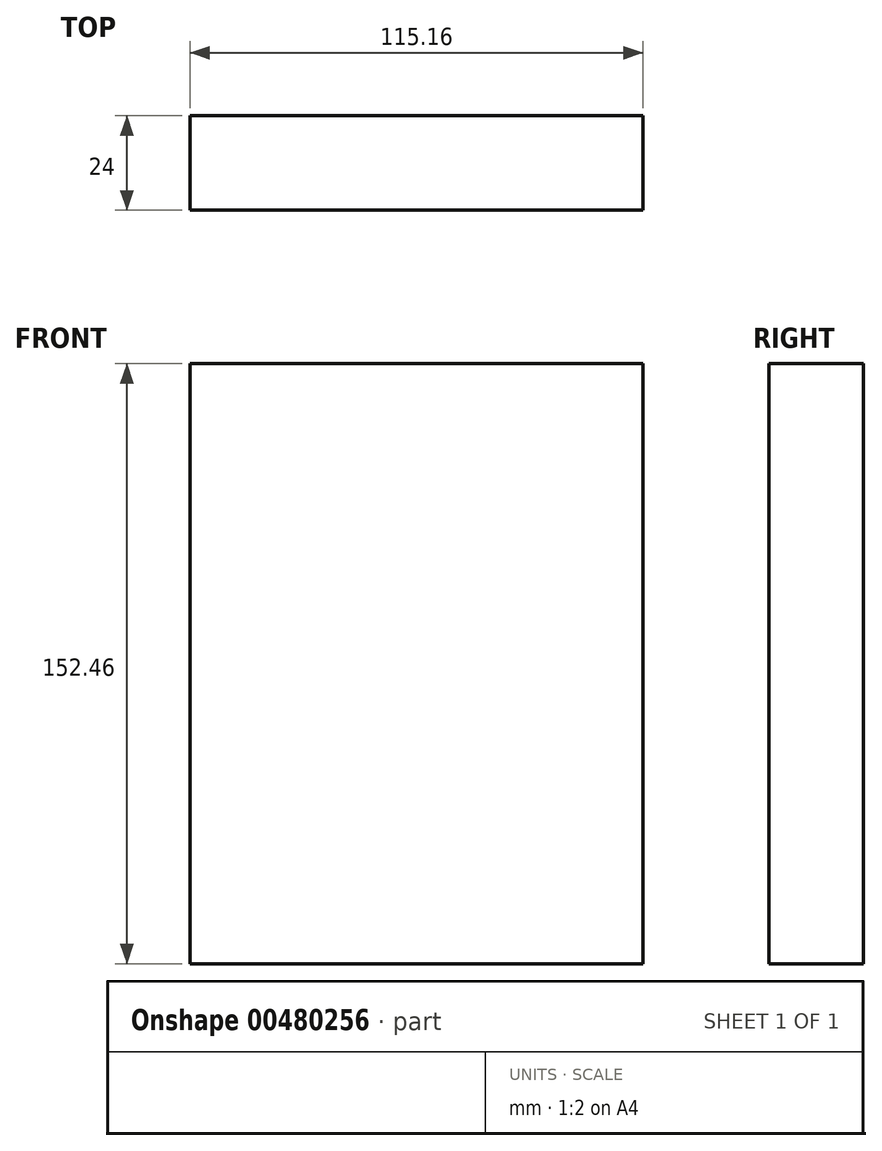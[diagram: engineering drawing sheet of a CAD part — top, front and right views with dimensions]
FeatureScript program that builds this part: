
annotation { "Feature Type Name" : "Feature", "Feature Type Description" : "" }
export const myFeature = defineFeature(function(context is Context, id is Id, definition is map)
    precondition{}
    {
        {
            var Q0;
            Q0=qCreatedBy(makeId("Front.planeOp"),FACE);
            var sketch = newSketch(context, id + "F0", { "sketchPlane" : qUnion([Q0])});
            skLineSegment(sketch, "E0.bottom", {"start": v(-57.58, 76.32) * mm, "end": v(57.58, 76.32) * mm});
            skLineSegment(sketch, "E0.top", {"start": v(-57.58, -76.14) * mm, "end": v(57.58, -76.14) * mm});
            skLineSegment(sketch, "E0.left", {"start": v(-57.58, 76.32) * mm, "end": v(-57.58, -76.14) * mm});
            skLineSegment(sketch, "E0.right", {"start": v(57.58, 76.32) * mm, "end": v(57.58, -76.14) * mm});
            skSolve(sketch);
        }
        {
            var Q0;
            Q0=makeQuery(id+"F0.imprint","IMPRINT",FACE,{"disambiguationData":[TD([[makeQuery(id+"F0.imprint","IMPRINT",EDGE,{"derivedFrom":sQuery(id+"F0.wireOp",EDGE,"E0.bottom")}),-1.0]])]});
            extrude(context, id + "F1", {"entities" : qUnion([Q0]), "depth" : 22 * mm, "hasSecondDirection" : true, "secondDirectionOppositeDirection" : true, "secondDirectionDepth" : 2 * mm});
        }
        {
            var Q0;
            Q0=qCreatedBy(makeId("Right.planeOp"),FACE);
            var sketch = newSketch(context, id + "F2", { "sketchPlane" : qUnion([Q0])});
            skLineSegment(sketch, "E1", {"start": v(0, 69.02) * mm, "end": v(0, -65.98) * mm});
            skArc(sketch, "E2", {"start": v(-17, -65.98) * mm, "mid": v(-8.5, -70.71) * mm, "end": v(0, -65.98) * mm});
            skLineSegment(sketch, "E3", {"start": v(-17, -65.98) * mm, "end": v(-19.1, -25.98) * mm});
            skSolve(sketch);
        }
        {
            var Q0;
            Q0=sQuery(id+"F2.wireOp",EDGE,"E1");
            var Q1;
            Q1=sQuery(id+"F2.wireOp",EDGE,"E2");
            var Q2;
            Q2=sQuery(id+"F2.wireOp",EDGE,"E3");
            extrude(context, id + "F3", {"bodyType" : ToolBodyType.SURFACE, "surfaceEntities" : qUnion([Q0, Q1, Q2]), "endBound" : BoundingType.SYMMETRIC, "depth" : 150 * mm});
        }
    });
